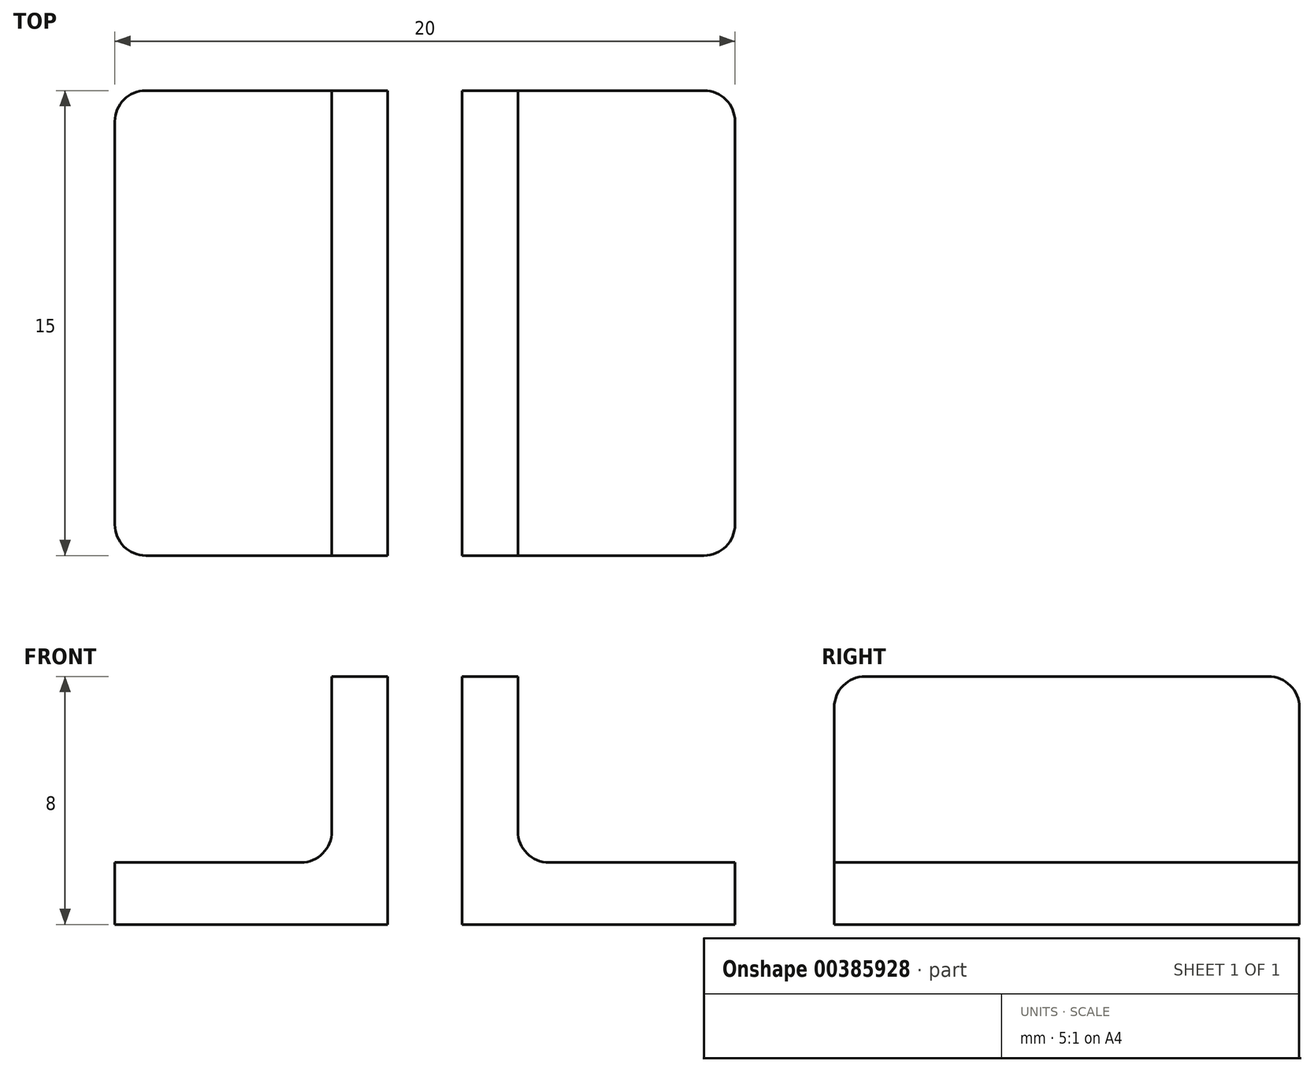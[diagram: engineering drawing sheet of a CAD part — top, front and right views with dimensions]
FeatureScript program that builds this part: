
annotation { "Feature Type Name" : "Feature", "Feature Type Description" : "" }
export const myFeature = defineFeature(function(context is Context, id is Id, definition is map)
    precondition{}
    {
        {
            var Q0;
            Q0=qCreatedBy(makeId("Top.planeOp"),FACE);
            var sketch = newSketch(context, id + "F0", { "sketchPlane" : qUnion([Q0])});
            skLineSegment(sketch, "E0.bottom", {"start": v(10, -7.5) * mm, "end": v(-10, -7.5) * mm});
            skLineSegment(sketch, "E0.top", {"start": v(10, 7.5) * mm, "end": v(-10, 7.5) * mm});
            skLineSegment(sketch, "E0.left", {"start": v(10, -7.5) * mm, "end": v(10, 7.5) * mm});
            skLineSegment(sketch, "E0.right", {"start": v(-10, -7.5) * mm, "end": v(-10, 7.5) * mm});
            skPoint(sketch, "E0.middle", {"position": v(0, 0) * mm});
            skLineSegment(sketch, "E1.bottom", {"start": v(1.2, -7.5) * mm, "end": v(-1.2, -7.5) * mm});
            skLineSegment(sketch, "E1.top", {"start": v(1.2, 7.5) * mm, "end": v(-1.2, 7.5) * mm});
            skLineSegment(sketch, "E1.left", {"start": v(1.2, -7.5) * mm, "end": v(1.2, 7.5) * mm});
            skLineSegment(sketch, "E1.right", {"start": v(-1.2, -7.5) * mm, "end": v(-1.2, 7.5) * mm});
            skLineSegment(sketch, "E2", {"start": v(3, 7.5) * mm, "end": v(3, -7.5) * mm});
            skLineSegment(sketch, "E3", {"start": v(-3, 7.5) * mm, "end": v(-3, -7.5) * mm});
            skSolve(sketch);
        }
        {
            var Q0;
            {var subQ0=sQuery(id+"F0.wireOp",EDGE,"E0.right");Q0=makeQuery(id+"F0.imprint","IMPRINT",FACE,{"disambiguationData":[TD([[makeQuery(id+"F0.imprint","IMPRINT",EDGE,{"derivedFrom":subQ0}),-1.0]])]});}
            var Q1;
            {var subQ0=sQuery(id+"F0.wireOp",EDGE,"E1.right");Q1=makeQuery(id+"F0.imprint","IMPRINT",FACE,{"disambiguationData":[TD([[makeQuery(id+"F0.imprint","IMPRINT",EDGE,{"derivedFrom":subQ0}),1.0]])]});}
            var Q2;
            Q2=makeQuery(id+"F0.imprint","IMPRINT",FACE,{"disambiguationData":[TD([[makeQuery(id+"F0.imprint","IMPRINT",EDGE,{"derivedFrom":sQuery(id+"F0.wireOp",EDGE,"E1.bottom")}),-1.0]])]});
            var Q3;
            {var subQ0=sQuery(id+"F0.wireOp",EDGE,"E1.left");Q3=makeQuery(id+"F0.imprint","IMPRINT",FACE,{"disambiguationData":[TD([[makeQuery(id+"F0.imprint","IMPRINT",EDGE,{"derivedFrom":subQ0}),-1.0]])]});}
            var Q4;
            {var subQ0=sQuery(id+"F0.wireOp",EDGE,"E0.left");Q4=makeQuery(id+"F0.imprint","IMPRINT",FACE,{"disambiguationData":[TD([[makeQuery(id+"F0.imprint","IMPRINT",EDGE,{"derivedFrom":subQ0}),1.0]])]});}
            extrude(context, id + "F1", {"entities" : qUnion([Q0, Q1, Q2, Q3, Q4]), "depth" : 2 * mm});
        }
        {
            var Q0;
            {var subQ0=sQuery(id+"F0.wireOp",EDGE,"E1.right");Q0=makeQuery(id+"F0.imprint","IMPRINT",FACE,{"disambiguationData":[TD([[makeQuery(id+"F0.imprint","IMPRINT",EDGE,{"derivedFrom":subQ0}),1.0]])]});}
            var Q1;
            {var subQ0=sQuery(id+"F0.wireOp",EDGE,"E1.left");Q1=makeQuery(id+"F0.imprint","IMPRINT",FACE,{"disambiguationData":[TD([[makeQuery(id+"F0.imprint","IMPRINT",EDGE,{"derivedFrom":subQ0}),-1.0]])]});}
            extrude(context, id + "F2", {"entities" : qUnion([Q0, Q1]), "operationType" : NewBodyOperationType.ADD, "depth" : 8 * mm});
        }
        {
            var Q0;
            {var subQ0=sQuery(id+"F0.wireOp",EDGE,"E0.bottom");Q0=makeQuery(id+"F2.opExtrude","CAP_EDGE",EDGE,{"disambiguationData":[OSD([subQ0]),TDD([makeQuery(id+"F0.imprint","IMPRINT",EDGE,{"disambiguationData":[TD([[makeQuery(id+"F0.imprint","INTERSECT",VERTEX,{"derivedFrom":[subQ0,sQuery(id+"F0.wireOp",EDGE,"E2")]}),-1.0]])],"derivedFrom":subQ0})])],"isStart":false});}
            var Q1;
            {var subQ0=sQuery(id+"F0.wireOp",EDGE,"E0.bottom");Q1=makeQuery(id+"F2.opExtrude","CAP_EDGE",EDGE,{"disambiguationData":[OSD([subQ0]),TDD([makeQuery(id+"F0.imprint","IMPRINT",EDGE,{"disambiguationData":[TD([[makeQuery(id+"F0.imprint","INTERSECT",VERTEX,{"derivedFrom":[subQ0,sQuery(id+"F0.wireOp",EDGE,"E3")]}),1.0]])],"derivedFrom":subQ0})])],"isStart":false});}
            var Q2;
            {var subQ0=sQuery(id+"F0.wireOp",EDGE,"E0.top");Q2=makeQuery(id+"F2.opExtrude","CAP_EDGE",EDGE,{"disambiguationData":[OSD([subQ0]),TDD([makeQuery(id+"F0.imprint","IMPRINT",EDGE,{"disambiguationData":[TD([[makeQuery(id+"F0.imprint","INTERSECT",VERTEX,{"derivedFrom":[subQ0,sQuery(id+"F0.wireOp",EDGE,"E3")]}),1.0]])],"derivedFrom":subQ0})])],"isStart":false});}
            var Q3;
            {var subQ0=sQuery(id+"F0.wireOp",EDGE,"E0.top");Q3=makeQuery(id+"F2.opExtrude","CAP_EDGE",EDGE,{"disambiguationData":[OSD([subQ0]),TDD([makeQuery(id+"F0.imprint","IMPRINT",EDGE,{"disambiguationData":[TD([[makeQuery(id+"F0.imprint","INTERSECT",VERTEX,{"derivedFrom":[subQ0,sQuery(id+"F0.wireOp",EDGE,"E2")]}),-1.0]])],"derivedFrom":subQ0})])],"isStart":false});}
            var Q4;
            Q4=makeQuery(id+"F1.opExtrude","SWEPT_EDGE",EDGE,{"disambiguationData":[OSD([sQuery(id+"F0.wireOp",EDGE,"E0.bottom"),sQuery(id+"F0.wireOp",EDGE,"E0.left")])]});
            var Q5;
            Q5=makeQuery(id+"F1.opExtrude","SWEPT_EDGE",EDGE,{"disambiguationData":[OSD([sQuery(id+"F0.wireOp",EDGE,"E0.top"),sQuery(id+"F0.wireOp",EDGE,"E0.left")])]});
            var Q6;
            Q6=makeQuery(id+"F1.opExtrude","SWEPT_EDGE",EDGE,{"disambiguationData":[OSD([sQuery(id+"F0.wireOp",EDGE,"E0.bottom"),sQuery(id+"F0.wireOp",EDGE,"E0.right")])]});
            var Q7;
            Q7=makeQuery(id+"F1.opExtrude","SWEPT_EDGE",EDGE,{"disambiguationData":[OSD([sQuery(id+"F0.wireOp",EDGE,"E0.top"),sQuery(id+"F0.wireOp",EDGE,"E0.right")])]});
            var Q8;
            Q8=makeQuery(id+"F2.boolean.opBoolean","INTERSECT",EDGE,{"derivedFrom":[makeQuery(id+"F1.opExtrude","CAP_FACE",FACE,{"disambiguationData":[OSD([sQuery(id+"F0.wireOp",EDGE,"E0.bottom"),sQuery(id+"F0.wireOp",EDGE,"E0.top"),sQuery(id+"F0.wireOp",EDGE,"E0.left"),sQuery(id+"F0.wireOp",EDGE,"E0.right"),sQuery(id+"F0.wireOp",EDGE,"E1.bottom"),sQuery(id+"F0.wireOp",EDGE,"E1.top")])],"isStart":false}),makeQuery(id+"F2.opExtrude","SWEPT_FACE",FACE,{"disambiguationData":[OSD([sQuery(id+"F0.wireOp",EDGE,"E2")])]})]});
            var Q9;
            Q9=makeQuery(id+"F2.boolean.opBoolean","INTERSECT",EDGE,{"derivedFrom":[makeQuery(id+"F1.opExtrude","CAP_FACE",FACE,{"disambiguationData":[OSD([sQuery(id+"F0.wireOp",EDGE,"E0.bottom"),sQuery(id+"F0.wireOp",EDGE,"E0.top"),sQuery(id+"F0.wireOp",EDGE,"E0.left"),sQuery(id+"F0.wireOp",EDGE,"E0.right"),sQuery(id+"F0.wireOp",EDGE,"E1.bottom"),sQuery(id+"F0.wireOp",EDGE,"E1.top")])],"isStart":false}),makeQuery(id+"F2.opExtrude","SWEPT_FACE",FACE,{"disambiguationData":[OSD([sQuery(id+"F0.wireOp",EDGE,"E3")])]})]});
            fillet(context, id + "F3", {"entities" : qUnion([Q0, Q1, Q2, Q3, Q4, Q5, Q6, Q7, Q8, Q9]), "radius" : 1 * mm, "tangentPropagation" : true, "allowEdgeOverflow" : false});
        }
    });
